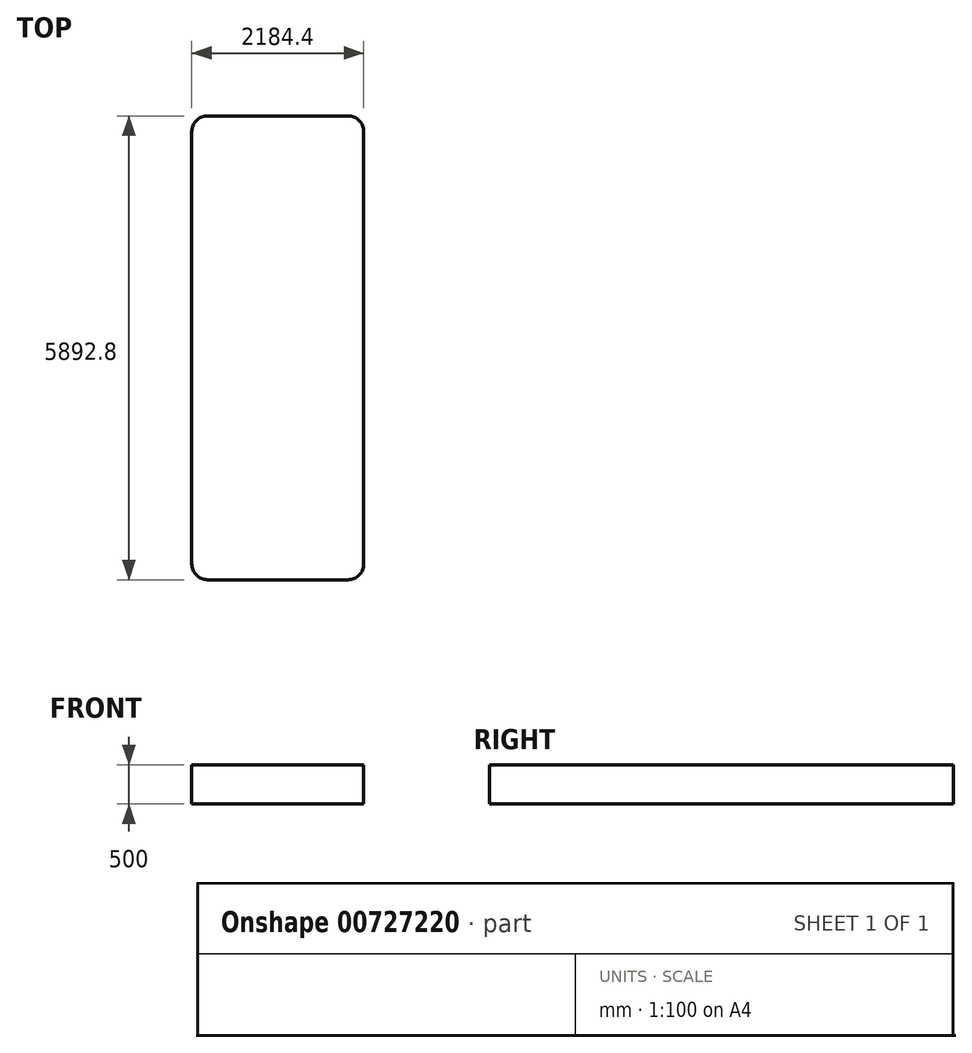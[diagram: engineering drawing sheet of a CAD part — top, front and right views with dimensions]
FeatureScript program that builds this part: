
annotation { "Feature Type Name" : "Feature", "Feature Type Description" : "" }
export const myFeature = defineFeature(function(context is Context, id is Id, definition is map)
    precondition{}
    {
        {
            var Q0;
            Q0=qCreatedBy(makeId("Top.planeOp"),FACE);
            var sketch = newSketch(context, id + "F0", { "sketchPlane" : qUnion([Q0])});
            skLineSegment(sketch, "E0.bottom", {"start": v(892.2, -2946.4) * mm, "end": v(-892.2, -2946.4) * mm});
            skLineSegment(sketch, "E0.top", {"start": v(892.2, 2946.4) * mm, "end": v(-892.2, 2946.4) * mm});
            skLineSegment(sketch, "E0.left", {"start": v(1092.2, -2746.4) * mm, "end": v(1092.2, 2746.4) * mm});
            skLineSegment(sketch, "E0.right", {"start": v(-1092.2, -2746.4) * mm, "end": v(-1092.2, 2746.4) * mm});
            skPoint(sketch, "E0.middle", {"position": v(0, 0) * mm});
            skPoint(sketch, "E1.visualSharp", {"position": v(-1092.2, 2946.4) * mm});
            skArc(sketch, "E1.filletArc", {"start": v(-892.2, 2946.4) * mm, "mid": v(-1033.62, 2887.82) * mm, "end": v(-1092.2, 2746.4) * mm});
            skPoint(sketch, "E2.visualSharp", {"position": v(1092.2, 2946.4) * mm});
            skArc(sketch, "E2.filletArc", {"start": v(1092.2, 2746.4) * mm, "mid": v(1033.62, 2887.82) * mm, "end": v(892.2, 2946.4) * mm});
            skPoint(sketch, "E3.visualSharp", {"position": v(1092.2, -2946.4) * mm});
            skArc(sketch, "E3.filletArc", {"start": v(892.2, -2946.4) * mm, "mid": v(1033.62, -2887.82) * mm, "end": v(1092.2, -2746.4) * mm});
            skPoint(sketch, "E4.visualSharp", {"position": v(-1092.2, -2946.4) * mm});
            skArc(sketch, "E4.filletArc", {"start": v(-1092.2, -2746.4) * mm, "mid": v(-1033.62, -2887.82) * mm, "end": v(-892.2, -2946.4) * mm});
            skSolve(sketch);
        }
        {
            var Q0;
            Q0=makeQuery(id+"F0.imprint","IMPRINT",FACE,{"disambiguationData":[TD([[makeQuery(id+"F0.imprint","IMPRINT",EDGE,{"derivedFrom":sQuery(id+"F0.wireOp",EDGE,"E0.bottom")}),-1.0]])]});
            extrude(context, id + "F1", {"entities" : qUnion([Q0]), "depth" : 500 * mm, "offsetDistance" : 25 * mm});
        }
    });
